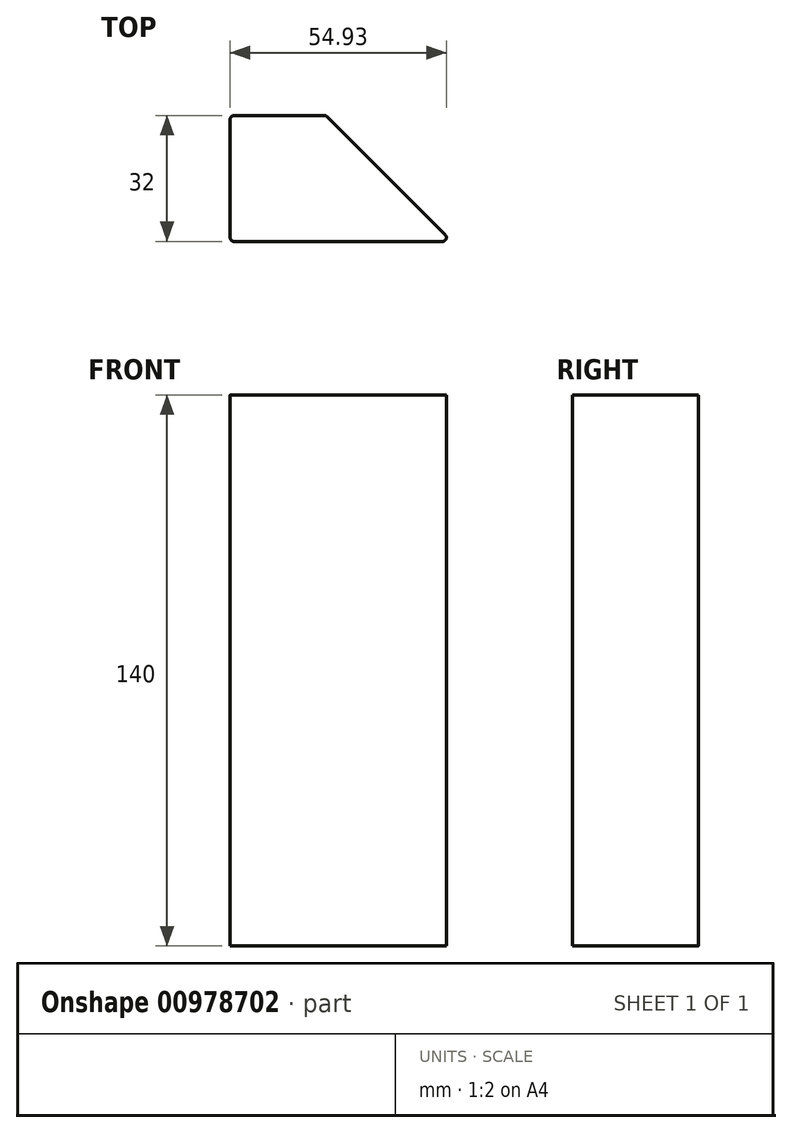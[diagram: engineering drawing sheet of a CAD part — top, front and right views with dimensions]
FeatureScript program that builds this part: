
annotation { "Feature Type Name" : "Feature", "Feature Type Description" : "" }
export const myFeature = defineFeature(function(context is Context, id is Id, definition is map)
    precondition{}
    {
        {
            var Q0;
            Q0=qCreatedBy(makeId("Top.planeOp"),FACE);
            var sketch = newSketch(context, id + "F0", { "sketchPlane" : qUnion([Q0])});
            skLineSegment(sketch, "E0", {"start": v(-67.3, 49.35) * mm, "end": v(-35.7, 49.35) * mm});
            skLineSegment(sketch, "E1", {"start": v(-32.17, 47.88) * mm, "end": v(10.95, 4.76) * mm});
            skLineSegment(sketch, "E2", {"start": v(9.54, 1.35) * mm, "end": v(-67.3, 1.35) * mm});
            skLineSegment(sketch, "E3", {"start": v(-69.3, 3.35) * mm, "end": v(-69.3, 47.35) * mm});
            skLineSegment(sketch, "E4.0", {"start": v(-64.3, 45.35) * mm, "end": v(-36.12, 45.35) * mm});
            skLineSegment(sketch, "E4.1", {"start": v(-65.3, 6.35) * mm, "end": v(-65.3, 44.35) * mm});
            skLineSegment(sketch, "E4.2", {"start": v(2.3, 5.35) * mm, "end": v(-64.3, 5.35) * mm});
            skLineSegment(sketch, "E4.3", {"start": v(-34.7, 44.76) * mm, "end": v(3, 7.05) * mm});
            skPoint(sketch, "E5.visualSharp", {"position": v(-33.63, 49.35) * mm});
            skArc(sketch, "E5.filletArc", {"start": v(-32.17, 47.88) * mm, "mid": v(-33.8, 48.97) * mm, "end": v(-35.7, 49.35) * mm});
            skPoint(sketch, "E6.visualSharp", {"position": v(-69.3, 49.35) * mm});
            skArc(sketch, "E6.filletArc", {"start": v(-67.3, 49.35) * mm, "mid": v(-68.7, 48.76) * mm, "end": v(-69.3, 47.35) * mm});
            skPoint(sketch, "E7.visualSharp", {"position": v(-65.3, 45.35) * mm});
            skArc(sketch, "E7.filletArc", {"start": v(-64.3, 45.35) * mm, "mid": v(-65, 45.05) * mm, "end": v(-65.3, 44.35) * mm});
            skPoint(sketch, "E8.visualSharp", {"position": v(-35.3, 45.35) * mm});
            skArc(sketch, "E8.filletArc", {"start": v(-34.7, 44.76) * mm, "mid": v(-35.35, 45.2) * mm, "end": v(-36.12, 45.35) * mm});
            skPoint(sketch, "E9.visualSharp", {"position": v(-69.3, 1.35) * mm});
            skArc(sketch, "E9.filletArc", {"start": v(-69.3, 3.35) * mm, "mid": v(-68.7, 1.93) * mm, "end": v(-67.3, 1.35) * mm});
            skPoint(sketch, "E10.visualSharp", {"position": v(14.37, 1.35) * mm});
            skArc(sketch, "E10.filletArc", {"start": v(9.54, 1.35) * mm, "mid": v(11.38, 2.58) * mm, "end": v(10.95, 4.76) * mm});
            skPoint(sketch, "E11.visualSharp", {"position": v(-65.3, 5.35) * mm});
            skArc(sketch, "E11.filletArc", {"start": v(-65.3, 6.35) * mm, "mid": v(-65, 5.64) * mm, "end": v(-64.3, 5.35) * mm});
            skPoint(sketch, "E12.visualSharp", {"position": v(4.7, 5.35) * mm});
            skArc(sketch, "E12.filletArc", {"start": v(2.3, 5.35) * mm, "mid": v(3.22, 5.96) * mm, "end": v(3, 7.05) * mm});
            skSolve(sketch);
        }
        {
            var Q0;
            Q0=makeQuery(id+"F0.imprint","IMPRINT",FACE,{"disambiguationData":[TD([[makeQuery(id+"F0.imprint","IMPRINT",EDGE,{"derivedFrom":sQuery(id+"F0.wireOp",EDGE,"E0")}),-1.0]])]});
            extrude(context, id + "F1", {"entities" : qUnion([Q0]), "depth" : 150 * mm, "offsetDistance" : 25 * mm});
        }
        {
            var Q0;
            Q0=qCreatedBy(makeId("Top.planeOp"),FACE);
            var sketch = newSketch(context, id + "F2", { "sketchPlane" : qUnion([Q0])});
            skLineSegment(sketch, "E13.0", {"start": v(-33.63, 49.35) * mm, "end": v(-69.3, 49.35) * mm});
            skLineSegment(sketch, "E13.1", {"start": v(-69.3, 49.35) * mm, "end": v(-69.3, 1.35) * mm});
            skLineSegment(sketch, "E13.2", {"start": v(-69.3, 1.35) * mm, "end": v(14.37, 1.35) * mm});
            skLineSegment(sketch, "E13.3", {"start": v(14.37, 1.35) * mm, "end": v(-33.63, 49.35) * mm});
            skLineSegment(sketch, "E14.0", {"start": v(-60.3, 41.35) * mm, "end": v(-37.36, 41.35) * mm});
            skLineSegment(sketch, "E14.1", {"start": v(-61.3, 10.35) * mm, "end": v(-61.3, 40.35) * mm});
            skLineSegment(sketch, "E14.2", {"start": v(-7.36, 9.35) * mm, "end": v(-60.3, 9.35) * mm});
            skLineSegment(sketch, "E14.3", {"start": v(-36.66, 41.05) * mm, "end": v(-6.66, 11.05) * mm});
            skPoint(sketch, "E15.visualSharp", {"position": v(-61.3, 41.35) * mm});
            skArc(sketch, "E15.filletArc", {"start": v(-60.3, 41.35) * mm, "mid": v(-61, 41.05) * mm, "end": v(-61.3, 40.35) * mm});
            skPoint(sketch, "E16.visualSharp", {"position": v(-36.95, 41.35) * mm});
            skArc(sketch, "E16.filletArc", {"start": v(-36.66, 41.05) * mm, "mid": v(-36.98, 41.27) * mm, "end": v(-37.36, 41.35) * mm});
            skPoint(sketch, "E17.visualSharp", {"position": v(-4.95, 9.35) * mm});
            skArc(sketch, "E17.filletArc", {"start": v(-7.36, 9.35) * mm, "mid": v(-6.44, 9.96) * mm, "end": v(-6.66, 11.05) * mm});
            skPoint(sketch, "E18.visualSharp", {"position": v(-61.3, 9.35) * mm});
            skArc(sketch, "E18.filletArc", {"start": v(-61.3, 10.35) * mm, "mid": v(-61, 9.64) * mm, "end": v(-60.3, 9.35) * mm});
            skSolve(sketch);
        }
        {
            var Q0;
            Q0=makeQuery(id+"F2.imprint","IMPRINT",FACE,{"disambiguationData":[TD([[makeQuery(id+"F2.imprint","IMPRINT",EDGE,{"derivedFrom":sQuery(id+"F2.wireOp",EDGE,"E14.0")}),-1.0]])]});
            extrude(context, id + "F3", {"entities" : qUnion([Q0]), "depth" : 140 * mm, "offsetDistance" : 25 * mm});
        }
        {
            var Q0;
            Q0=makeQuery(id+"F1.opExtrude","SWEPT_BODY",BODY,{"disambiguationData":[OSD([sQuery(id+"F0.wireOp",EDGE,"E0"),sQuery(id+"F0.wireOp",EDGE,"E1"),sQuery(id+"F0.wireOp",EDGE,"E2"),sQuery(id+"F0.wireOp",EDGE,"E3"),sQuery(id+"F0.wireOp",EDGE,"E4.0"),sQuery(id+"F0.wireOp",EDGE,"E4.1"),sQuery(id+"F0.wireOp",EDGE,"E4.2"),sQuery(id+"F0.wireOp",EDGE,"E4.3"),sQuery(id+"F0.wireOp",EDGE,"E5.filletArc"),sQuery(id+"F0.wireOp",EDGE,"E6.filletArc"),sQuery(id+"F0.wireOp",EDGE,"E7.filletArc"),sQuery(id+"F0.wireOp",EDGE,"E8.filletArc"),sQuery(id+"F0.wireOp",EDGE,"E9.filletArc"),sQuery(id+"F0.wireOp",EDGE,"E10.filletArc"),sQuery(id+"F0.wireOp",EDGE,"E11.filletArc"),sQuery(id+"F0.wireOp",EDGE,"E12.filletArc")])]});
            deleteBodies(context, id + "F4", {"entities" : qUnion([Q0])});
        }
    });
